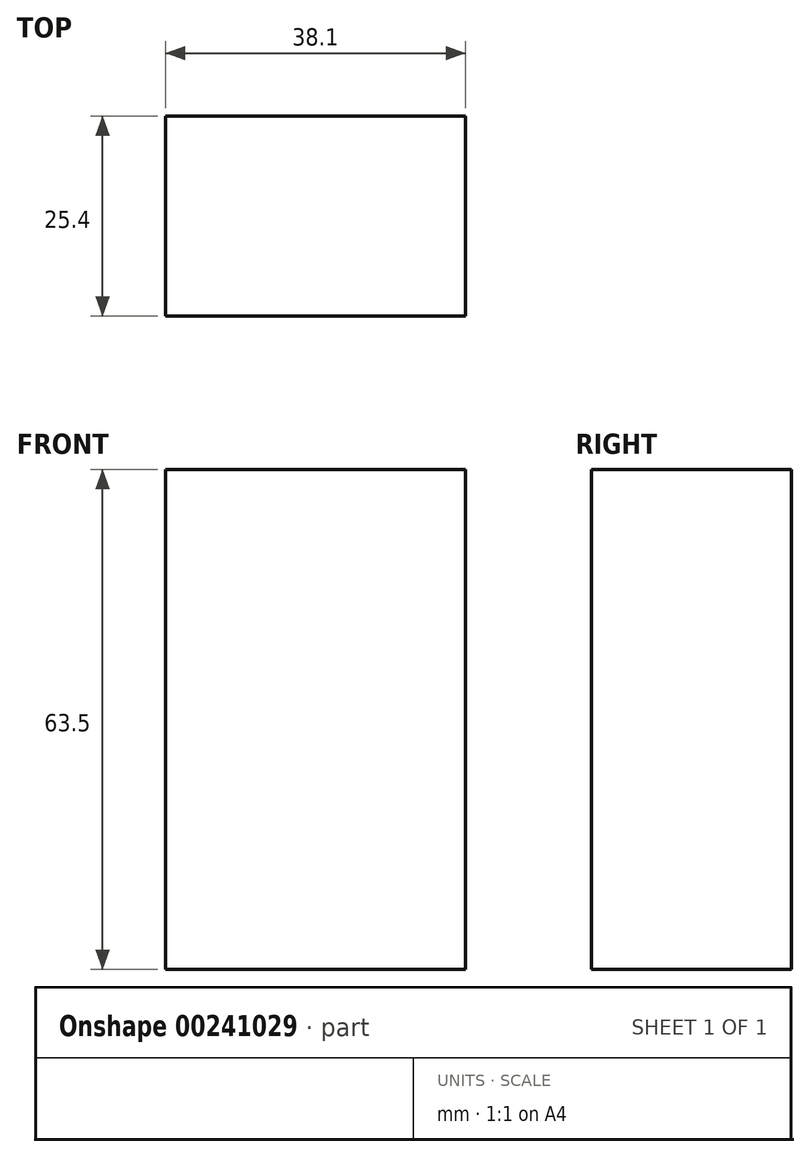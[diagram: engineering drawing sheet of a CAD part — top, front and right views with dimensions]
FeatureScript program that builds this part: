
annotation { "Feature Type Name" : "Feature", "Feature Type Description" : "" }
export const myFeature = defineFeature(function(context is Context, id is Id, definition is map)
    precondition{}
    {
        {
            var Q0;
            Q0=qCreatedBy(makeId("Front.planeOp"),FACE);
            var sketch = newSketch(context, id + "F0", { "sketchPlane" : qUnion([Q0])});
            skLineSegment(sketch, "E0.bottom", {"start": v(0, 0) * mm, "end": v(-38.1, 0) * mm});
            skLineSegment(sketch, "E0.top", {"start": v(0, 63.5) * mm, "end": v(-38.1, 63.5) * mm});
            skLineSegment(sketch, "E0.left", {"start": v(0, 0) * mm, "end": v(0, 63.5) * mm});
            skLineSegment(sketch, "E0.right", {"start": v(-38.1, 0) * mm, "end": v(-38.1, 63.5) * mm});
            skSolve(sketch);
        }
        {
            var Q0;
            Q0 = qSketchRegion(id + "F0", true);
            extrude(context, id + "F1", {"entities" : qUnion([Q0]), "depth" : 25.4 * mm});
        }
    });
